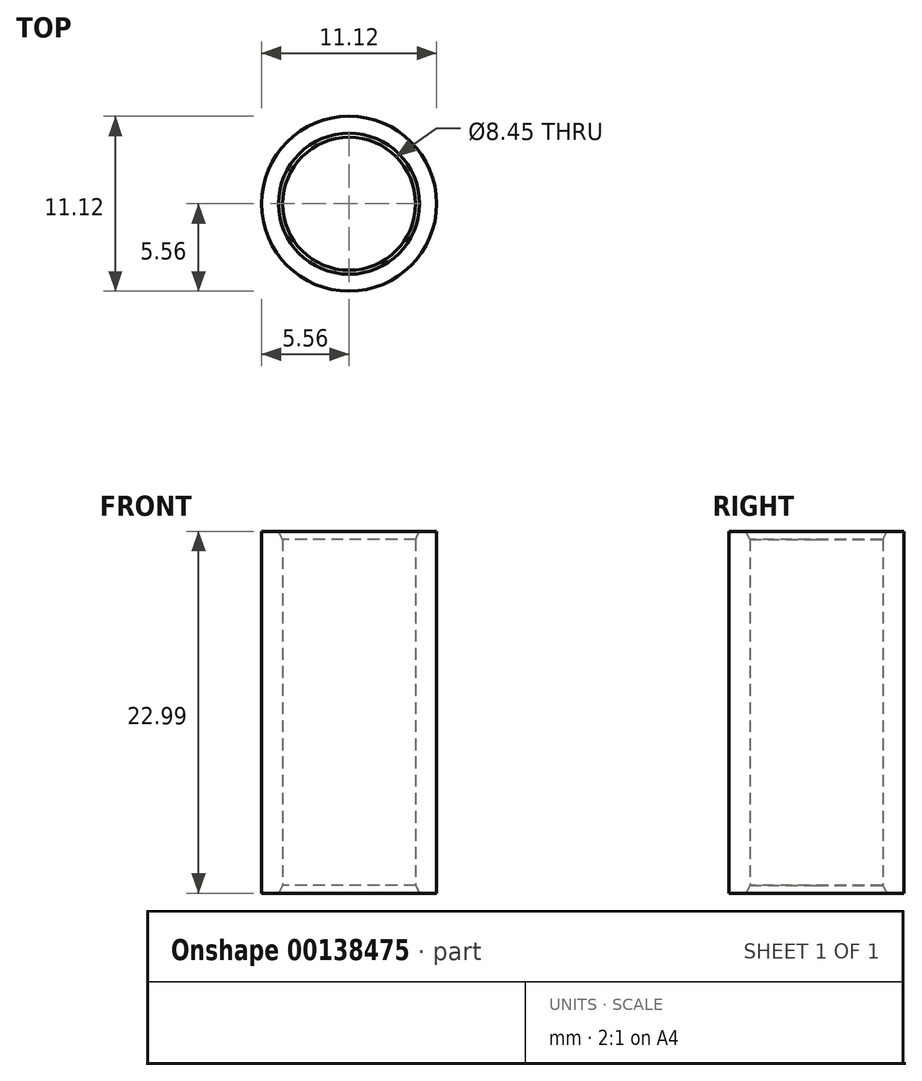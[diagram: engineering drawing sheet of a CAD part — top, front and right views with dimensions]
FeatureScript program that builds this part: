
annotation { "Feature Type Name" : "Feature", "Feature Type Description" : "" }
export const myFeature = defineFeature(function(context is Context, id is Id, definition is map)
    precondition{}
    {
        {
            var Q0;
            Q0=qCreatedBy(makeId("Top.planeOp"),FACE);
            var sketch = newSketch(context, id + "F0", { "sketchPlane" : qUnion([Q0])});
            skCircle(sketch, "E0", {"center": v(0, 0) * mm, "radius": 5.56 * mm});
            skCircle(sketch, "E1", {"center": v(0, 0) * mm, "radius": 4.22 * mm});
            skSolve(sketch);
        }
        {
            var Q0;
            Q0 = qSketchRegion(id + "F0", true);
            extrude(context, id + "F1", {"entities" : qUnion([Q0]), "depth" : 23 * mm});
        }
        {
            var Q0;
            Q0=makeQuery(id+"F1.opExtrude","CAP_EDGE",EDGE,{"disambiguationData":[OSD([sQuery(id+"F0.wireOp",EDGE,"E1")])],"isStart":false});
            var Q1;
            Q1=makeQuery(id+"F1.opExtrude","CAP_EDGE",EDGE,{"disambiguationData":[OSD([sQuery(id+"F0.wireOp",EDGE,"E1")])],"isStart":true});
            chamfer(context, id + "F2", {"entities" : qUnion([Q0, Q1]), "chamferType" : ChamferType.TWO_OFFSETS, "width1" : 0.5 * mm, "oppositeDirection" : false, "width2" : 0.25 * mm, "tangentPropagation" : true});
        }
    });
